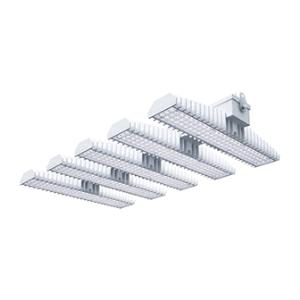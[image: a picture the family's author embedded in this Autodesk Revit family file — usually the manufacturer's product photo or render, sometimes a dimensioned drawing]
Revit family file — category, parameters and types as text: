
# Revit family: 3f_filippi_-_3f_lem_ho_medio_3f_filippi_-_58969_a0811_-_3f_lem_5_ho_led_350_cr_medio___vt_7048
name_source: partatom
category: Lighting Fixtures
units: mm (PartAtom-declared; Revit-internal decimal feet)

## family parameters
Cut with Voids When Loaded = No
Host = Face
Light Source = No
Part Type = Normal
Room Calculation Point = No
Round Connector Dimension = Use Diameter
Shared = No

## types (1)
- 3F Filippi - 3F LEM HO Medio (1 x LED, 51492 lm, 345 W, 4000 K)
    Apparent Load = 345 VA
    Approval mark = CE
    CIE Flux Codes = 83 96 99 100 100
    Color Rendering = 80
    Color Temperature = 4000 K
    Control Gear = Electronic ballast
    Default Elevation = 1800 mm
    Description = Industrial luminaire with high light output and high luminous efficiency designed with the most innovative technologies for environments with temperature up to 55°C.

ILLUMINOTECHNICAL
Luminous efficiency 100% (DLOR 99%, ULOR 1%).
Initial luminous flux of the luminaire 51492 lm.
Medium distribution with rectangular shape.
Installation Interdistance Transv.D = 1.02 x hu - Long.D = 1.06 x hu.
Tabular UGR (CIE 117 - 4H-8H; S=0.25H; 70/50/20): RUG 19.9 - 19.5.
Beam angle: 65° - 67°.
Luminous efficacy 149 lm/W.
Lifetime (L93/B10): 30000 h. (tq+25°C)
Lifetime (L90/B10): 50000 h. (tq+25°C)
Lifetime (L85/B10): 80000 h. (tq+25°C)
Lifetime (L80/B10): 100000 h. (tq+25°C)
Lifetime (L85/B10): 50000 h. (tq+55°C)
Sudden decreased luminous flux after 50000 hours: 0% (C0).
Photobiological safety in compliance with IEC/TR 62778: RG0 risk exempt, (IEC 62471).
In compliance with IEC/EN 62722-2-1 - IEC/EN 62717 standards.

SOURCE
5 Mid-Power linear LED modules 70W/840.
Energy efficiency class (UE 2019/2020 - UE 2019/2015): C.
CIE 13.3 Colour rendering index: CRI >80 (R9 <50%).
IES TM-30 Fidelity Index: Rf = 84 Rg = 95.
CCT nominal colour temperature 4000 K.
Colour initial tolerance (MacAdam): SDCM 3.

MECHANICAL
Passive modular heatsinks in die-casted aluminium, painted in white colour.
To optimize the thermal management of the LED module, the heatsinks are oversized and provided with self-cleaning of cooling fins.
Wiring body in aluminium and galvanised steel anchored solidly to the sinks and thermally separated.
3F Lens lenses with high luminous efficiency, transparent methacrylate (PMMA), fixed to the LED modules.
Fixing brackets in stainless steel.
Luminaire with limited surface temperature. - D - (EN 60598-2-24)
Dimensions: 952x542 mm, height 133 mm. Weight 24.14 kg.
IP65 protection degree.
Mechanical strength to impacts IK06 (1 joule).
Glow-wire test resistance 650°C.

ELECTRICAL
Halogen Free electronic wiring 230V-50/60Hz, power factor 0.97, THD <25%, constant output current, class I, 3 driver.
Power of the luminaire 345 W.
ENEC - CE.
SAFE FLICKER: PstLM=<1 and SVM=<0.4 (IEC TR 61547-1 and IEC TR 63158), to ensure a more comfortable and safe light.
Luminaire compliant with EN 60598-2-22 for power supply from a centralised emergency system CPSS (Central Power Supply System), not incorporated in the luminaire - high risk areas excluded. The default power and flux are 100% in AC and 100% in DC.
Ambient temperature from -30°C to +55°C.
Temperature class T6 max 85°C.
Quick connection via M20 3P connector with 9-13 mm tightening range.
Power unit positioned on a separate compartment by the LED module to ensure optimum temperatures of cabling components, to be inspectable and maintainable.
Relative humidity UR: <85%.

INSTALLATION
Ceiling / Suspended / Wall.
All accessories dedicated to this product are available on the Catalog and on our website www.3F-Filippi.com.

ACCESSORIES
A0811 - VT transparent glass, tempered, not flammable, with sealing gasket.
One required for each light module. The pack contains 10 pieces.

APPLICATIONS
In commercial environments, exhibition and industrial areas, stores, open areas.
Environments in which it is necessary a total protection against falling fragments (eg environments with foodstuffs or machines with moving parts or with extreme temperature changes), use luminaires with polycarbonate lenses.

WARNING
Fixture not suitable for cold stores with an ambient temperature <0°C and/or relative humidity >85%.
Luminaire designed for disposal/recycling at end-of-life.
Replaceable (LED only) light source by a professional. Replaceable control gear by a professional.
    Height = 133 mm  [stored 0.436352 ft]
    Lamp = 1 x LED
    Lamp Light Flux = 51492 lm
    Lamp Power = 345 W
    Lamp count = 1
    Length = 952 mm
    Lifetime = 50000 h
    Luminous efficacy = 149 lm/W
    Manufacturer = 3F Filippi
    ModVariant = No
    Model = 3F Filippi - 58969+A0811 - 3F LEM 5 HO LED 350 CR MEDIO + VT
    Mounting Place = Ceiling
    Mounting Type = Pendant
    Number of Poles = 1
    OnlyDefault = Yes
    Power Factor = 1
    Product Name = 3F Filippi - 3F LEM HO Medio
    Product group = pendant luminaire
    ProductGroupID = 9
    Protection Class = Protection class I
    Protection Degree = IP 65
    RLX_Detail_Level = 1
    RLX_Emergency_Light_Flux = 0 lm
    RLX_Emergency_Type = 0
    RLX_Emergency_Type_DB = No
    RlxData = <blob elided: 126385 chars, md5=8c328bee>
    Socket = socket
    Standby Power = 0 W
    System Light Flux = 51492 lm
    System Power = 345 W
    Type Comments = Product without accessories
    Type Image = 3f_filippi_-_lem_5__a0811.jpg
    URL = http://relux.com
    VarID = ---
    Voltage = 0 V
    Weight = 0.00 kg
    Width = 542 mm

note: [stored X ft] marks values corroborated as IEEE doubles in the binary element streams (Revit-internal decimal feet)

## geometry (parser evidence)
native form markers: Blend x4, Sweep x12
no freeform markers — native parametric forms only
